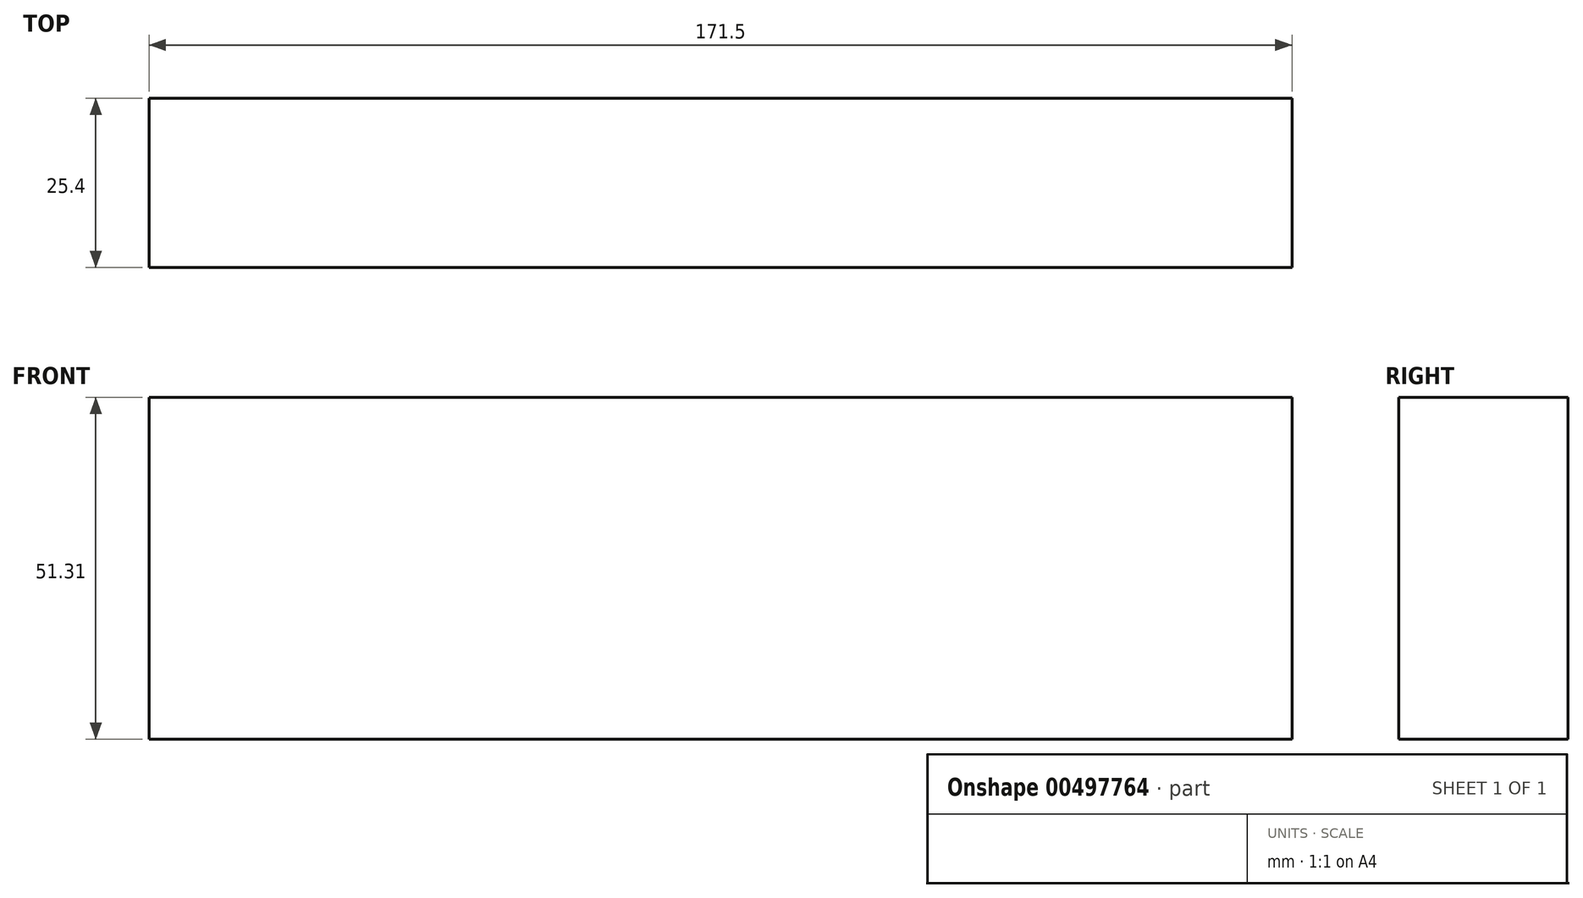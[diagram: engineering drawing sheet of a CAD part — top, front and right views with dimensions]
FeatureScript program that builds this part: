
annotation { "Feature Type Name" : "Feature", "Feature Type Description" : "" }
export const myFeature = defineFeature(function(context is Context, id is Id, definition is map)
    precondition{}
    {
        {
            var Q0;
            Q0=qCreatedBy(makeId("Front.planeOp"),FACE);
            var sketch = newSketch(context, id + "F0", { "sketchPlane" : qUnion([Q0])});
            skLineSegment(sketch, "E0.bottom", {"start": v(57.65, -22.47) * mm, "end": v(-113.85, -22.47) * mm});
            skLineSegment(sketch, "E0.top", {"start": v(57.65, 28.84) * mm, "end": v(-113.85, 28.84) * mm});
            skLineSegment(sketch, "E0.left", {"start": v(57.65, -22.47) * mm, "end": v(57.65, 28.84) * mm});
            skLineSegment(sketch, "E0.right", {"start": v(-113.85, -22.47) * mm, "end": v(-113.85, 28.84) * mm});
            skPoint(sketch, "E0.middle", {"position": v(-28.1, 3.19) * mm});
            skSolve(sketch);
        }
        {
            var Q0;
            Q0 = qSketchRegion(id + "F0", true);
            extrude(context, id + "F1", {"entities" : qUnion([Q0]), "depth" : 25.4 * mm});
        }
    });
